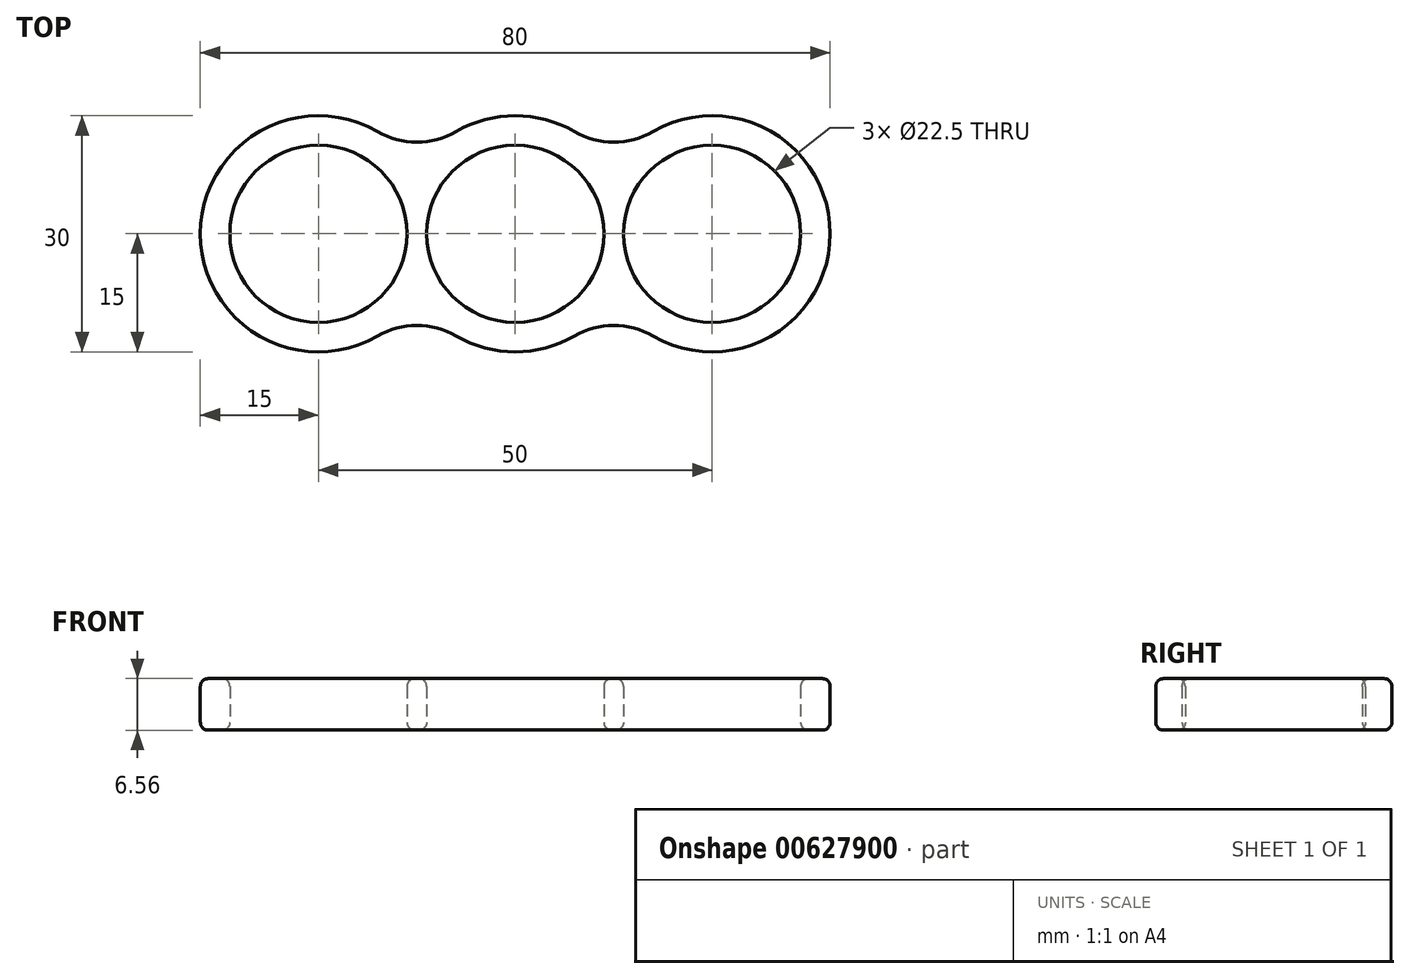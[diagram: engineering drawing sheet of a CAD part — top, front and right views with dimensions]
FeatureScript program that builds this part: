
annotation { "Feature Type Name" : "Feature", "Feature Type Description" : "" }
export const myFeature = defineFeature(function(context is Context, id is Id, definition is map)
    precondition{}
    {
        {
            var Q0;
            Q0=qCreatedBy(makeId("Top.planeOp"),FACE);
            var sketch = newSketch(context, id + "F0", { "sketchPlane" : qUnion([Q0])});
            skCircle(sketch, "E0", {"center": v(0, 0) * mm, "radius": 11.25 * mm});
            skCircle(sketch, "E1", {"center": v(-25, 0) * mm, "radius": 11.25 * mm});
            skPoint(sketch, "E2.0.midPoint", {"position": v(10, 0) * mm});
            skPoint(sketch, "E3.MirrorP", {"position": v(-10, 0) * mm});
            skPoint(sketch, "E4.orphan", {"position": v(0, -17.32) * mm});
            skPoint(sketch, "E5.orphan", {"position": v(0, 17.32) * mm});
            skArc(sketch, "E6", {"start": v(-7.5, -13) * mm, "mid": v(0, -15) * mm, "end": v(7.5, -13) * mm});
            skArc(sketch, "E7", {"start": v(-17.5, 13) * mm, "mid": v(-40, 0) * mm, "end": v(-17.5, -13) * mm});
            skArc(sketch, "E8", {"start": v(-17.5, 13) * mm, "mid": v(-12.5, 11.65) * mm, "end": v(-7.5, 13) * mm});
            skArc(sketch, "E9", {"start": v(-7.5, -13) * mm, "mid": v(-12.5, -11.65) * mm, "end": v(-17.5, -13) * mm});
            skPoint(sketch, "E10.end.orphan", {"position": v(-2.73, 6.98) * mm});
            skPoint(sketch, "E10.start.orphan", {"position": v(2.73, 6.98) * mm});
            skCircle(sketch, "E11.MirrorC", {"center": v(25, 0) * mm, "radius": 11.25 * mm});
            skArc(sketch, "E12.MirrorCS", {"start": v(17.5, 13) * mm, "mid": v(12.5, 11.65) * mm, "end": v(7.5, 13) * mm});
            skArc(sketch, "E13.MirrorCS", {"start": v(17.5, 13) * mm, "mid": v(40, 0) * mm, "end": v(17.5, -13) * mm});
            skArc(sketch, "E14.MirrorCS", {"start": v(7.5, -13) * mm, "mid": v(0, -15) * mm, "end": v(-7.5, -13) * mm});
            skArc(sketch, "E15.MirrorCS", {"start": v(7.5, -13) * mm, "mid": v(12.5, -11.65) * mm, "end": v(17.5, -13) * mm});
            skArc(sketch, "E16.trimOffspring", {"start": v(-7.5, 13) * mm, "mid": v(0, 15) * mm, "end": v(7.5, 13) * mm});
            skArc(sketch, "E17.trimOffspring", {"start": v(7.5, 13) * mm, "mid": v(0, 15) * mm, "end": v(-7.5, 13) * mm});
            skSolve(sketch);
        }
        {
            var Q0;
            Q0 = qSketchRegion(id + "F0", true);
            extrude(context, id + "F1", {"entities" : qUnion([Q0]), "endBound" : BoundingType.SYMMETRIC, "depth" : 6.55 * mm, "offsetDistance" : 25 * mm});
        }
        {
            var Q0;
            Q0=makeQuery(id+"F1.opExtrude","CAP_FACE",FACE,{"disambiguationData":[OSD([sQuery(id+"F0.wireOp",EDGE,"E1"),sQuery(id+"F0.wireOp",EDGE,"E7"),sQuery(id+"F0.wireOp",EDGE,"E8"),sQuery(id+"F0.wireOp",EDGE,"E9"),sQuery(id+"F0.wireOp",EDGE,"E11.MirrorC"),sQuery(id+"F0.wireOp",EDGE,"E12.MirrorCS"),sQuery(id+"F0.wireOp",EDGE,"E13.MirrorCS"),sQuery(id+"F0.wireOp",EDGE,"E0"),sQuery(id+"F0.wireOp",EDGE,"E14.MirrorCS"),sQuery(id+"F0.wireOp",EDGE,"E15.MirrorCS"),sQuery(id+"F0.wireOp",EDGE,"E17.trimOffspring")])],"isStart":false});
            fillet(context, id + "F2", {"entities" : qUnion([Q0]), "radius" : 1 * mm, "tangentPropagation" : true, "allowEdgeOverflow" : false});
        }
        {
            var Q0;
            Q0=makeQuery(id+"F1.opExtrude","CAP_FACE",FACE,{"disambiguationData":[OSD([sQuery(id+"F0.wireOp",EDGE,"E1"),sQuery(id+"F0.wireOp",EDGE,"E7"),sQuery(id+"F0.wireOp",EDGE,"E8"),sQuery(id+"F0.wireOp",EDGE,"E9"),sQuery(id+"F0.wireOp",EDGE,"E11.MirrorC"),sQuery(id+"F0.wireOp",EDGE,"E12.MirrorCS"),sQuery(id+"F0.wireOp",EDGE,"E13.MirrorCS"),sQuery(id+"F0.wireOp",EDGE,"E0"),sQuery(id+"F0.wireOp",EDGE,"E14.MirrorCS"),sQuery(id+"F0.wireOp",EDGE,"E15.MirrorCS"),sQuery(id+"F0.wireOp",EDGE,"E17.trimOffspring")])],"isStart":true});
            fillet(context, id + "F3", {"entities" : qUnion([Q0]), "radius" : 1 * mm, "tangentPropagation" : true, "allowEdgeOverflow" : false});
        }
    });
